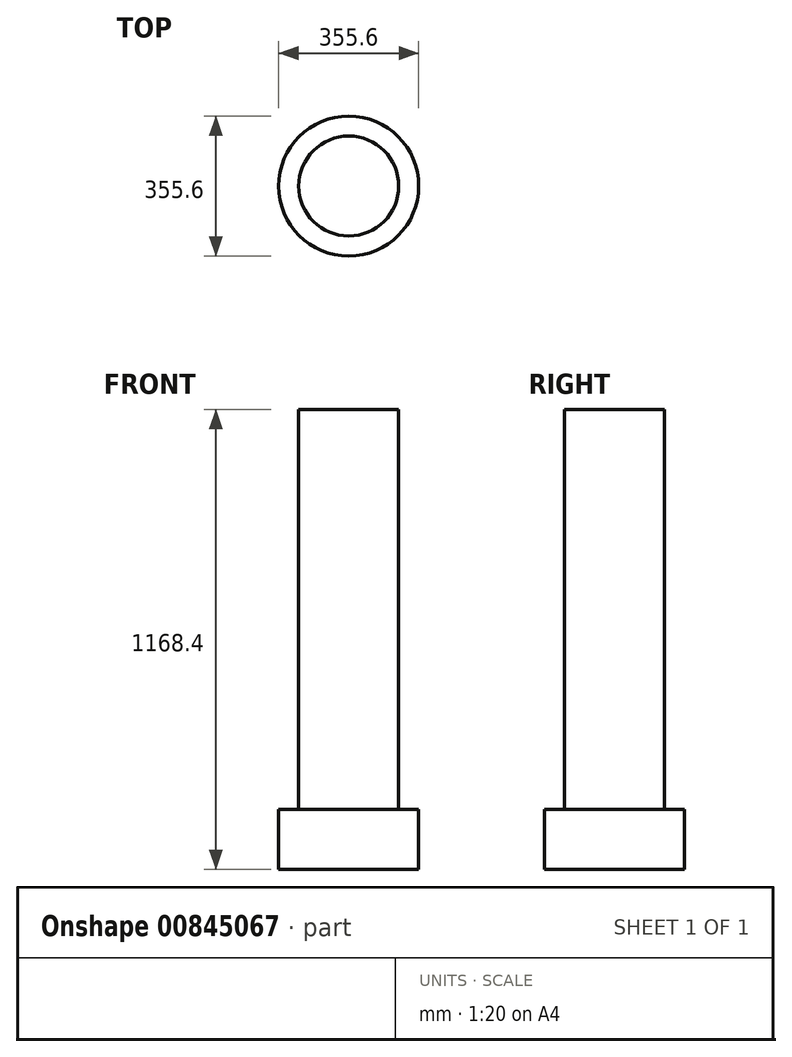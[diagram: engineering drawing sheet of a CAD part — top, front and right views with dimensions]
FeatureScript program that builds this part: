
annotation { "Feature Type Name" : "Feature", "Feature Type Description" : "" }
export const myFeature = defineFeature(function(context is Context, id is Id, definition is map)
    precondition{}
    {
        {
            var Q0;
            Q0=qCreatedBy(makeId("Front.planeOp"),FACE);
            var sketch = newSketch(context, id + "F0", { "sketchPlane" : qUnion([Q0])});
            skLineSegment(sketch, "E0", {"start": v(0, 431.87) * mm, "end": v(0, -503.6) * mm, "construction": true});
            skLineSegment(sketch, "E1", {"start": v(0, 1016) * mm, "end": v(127, 1016) * mm});
            skLineSegment(sketch, "E2", {"start": v(127, 1016) * mm, "end": v(127, 0) * mm});
            skLineSegment(sketch, "E3", {"start": v(127, 0) * mm, "end": v(177.8, 0) * mm});
            skLineSegment(sketch, "E4", {"start": v(177.8, 0) * mm, "end": v(177.8, -152.4) * mm});
            skLineSegment(sketch, "E5", {"start": v(177.8, -152.4) * mm, "end": v(0, -152.4) * mm});
            skLineSegment(sketch, "E6", {"start": v(0, -152.4) * mm, "end": v(0, 1016) * mm});
            skSolve(sketch);
        }
        {
            var Q0;
            Q0 = qSketchRegion(id + "F0", true);
            var Q1;
            Q1=sQuery(id+"F0.wireOp",EDGE,"E0");
            revolve(context, id + "F1", {"surfaceOperationType" : NewSurfaceOperationType.NEW, "entities" : qUnion([Q0]), "axis" : qUnion([Q1]), "revolveType" : RevolveType.FULL});
        }
    });
